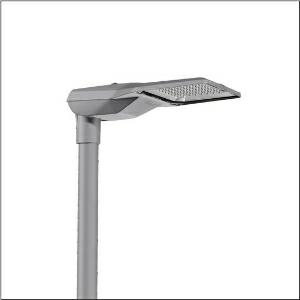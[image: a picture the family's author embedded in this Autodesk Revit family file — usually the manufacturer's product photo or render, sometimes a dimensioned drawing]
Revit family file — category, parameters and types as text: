
# Revit family: streetlight_sl_21_iq_midi___st1_0ab_5xe3m31v08nb_f534
name_source: partatom
category: Lighting Fixtures
units: mm (PartAtom-declared; Revit-internal decimal feet)

## family parameters
Cut with Voids When Loaded = No
Host = Face
Light Source = No
Part Type = Normal
Room Calculation Point = No
Round Connector Dimension = Use Diameter
Shared = No

## types (1)
- --- (1 x LED, 18970 lm, 136.6 W, 3000K)
    Apparent Load = 137 VA
    CIE Flux Codes = 40 74 97 100 100
    Color Rendering = 70
    Color Temperature = 3000K
    Default Elevation = 1800 mm
    Description = Streetlight SL 21 iQ midi, mast luminaire, primary light control with lens, of PMMA, primary optical cover: cover, of toughened safety glass, transparent, light distribution: ST1.0aB, light emission: direct distribution, primary light characteristic: asymmetric, installation type: post-top, side-entry, LED, High Power LED, rated luminous flux: 18.970lm, luminous efficacy: 139lm/W, light colour: 730, colour temperature: 3000K, control gear: iQ-Street Remote, D4i with power reduction, control: pre-setting: logarithmic dimming characteristic, Street-Remote, Auto-Match, Temp-Guard, Lumen-Switch, Night-Set, Smart-Wire, Light-Fading, Desk-Remote (wireless, voltage-free reading and setting of iQ features in the workshop via application-optimized NFC function/RFID function), optimised constant luminous flux control (CLO 2.0), mains connection: 230..240V, AC, 50/60Hz, start of lifetime: 137W, end of service life: 144W, reduction: 61W, luminaire housing, of diecast aluminium, powder-coated, Siteco® metallic grey (DB 702S), corrosivity category C5 mid according to DIN EN ISO 12944, please order mast flange separately, inclination adjustable: 0°, 5°, 10°, 15°, sealing non-destructively replaceable, multi-level sealing system, length: 644mm, width: 335mm, height: 110mm, mast flange for spigot size: 42mm (side-entry): 5XC10008XM4, 60/48mm (side-entry/post-top): 5XC10108XM2, 76/60mm (side-entry/post-top): 5XC10108XM1, mounting height: 4..8m, Smart Interface above, protection rating (complete): IP66, insulation class (complete): insulation class II (safety insulation), certification: CE, ENEC, ENEC+, VDE, impact resistance: IK10, permissible operating ambient temperature for outdoor applications: -40..+50°C, standard-compliant lighting for roads and squares, packaging unit: 1 piece

Light Distribution: ST1.0aB
    Height = 111 mm
    Lamp = 1 x LED
    Lamp Light Flux = 18970 lm
    Lamp Power = 136.6 W
    Lamp count = 1
    Length = 644 mm
    Luminous efficacy = 139 lm/W
    Manufacturer = Siteco
    ModVariant = No
    Model = 5XE3M31V08NB
    Number of Poles = 1
    OnlyDefault = Yes
    Power Factor = 1
    Product Name = Streetlight SL 21 iQ midi | ST1.0aB
    Product group = mast luminaire | pylon top
    ProductGroupID = 6100
    Protection Class = Protection class II
    Protection Degree = IP 66
    RLX_Detail_Level = 1
    RLX_Emergency_Light_Flux = 0 lm
    RLX_Emergency_Type = 0
    RLX_Emergency_Type_DB = No
    RlxData = <blob elided: 91685 chars, md5=901c0361>
    Socket = socket
    Standby Power = 0 W
    System Light Flux = 18970 lm
    System Power = 137 W
    Type Comments = factory setting: luminous flux: 100 % | dim-lin: 254 | 733 mA
    Type Image = l_1004302.jpg
    URL = http://relux.com
    VarID = @adj_133573
    Voltage = 0 V
    Weight = 0.00 kg
    Width = 336 mm

## geometry (parser evidence)
native form markers: Blend x4, Sweep x10
no freeform markers — native parametric forms only
